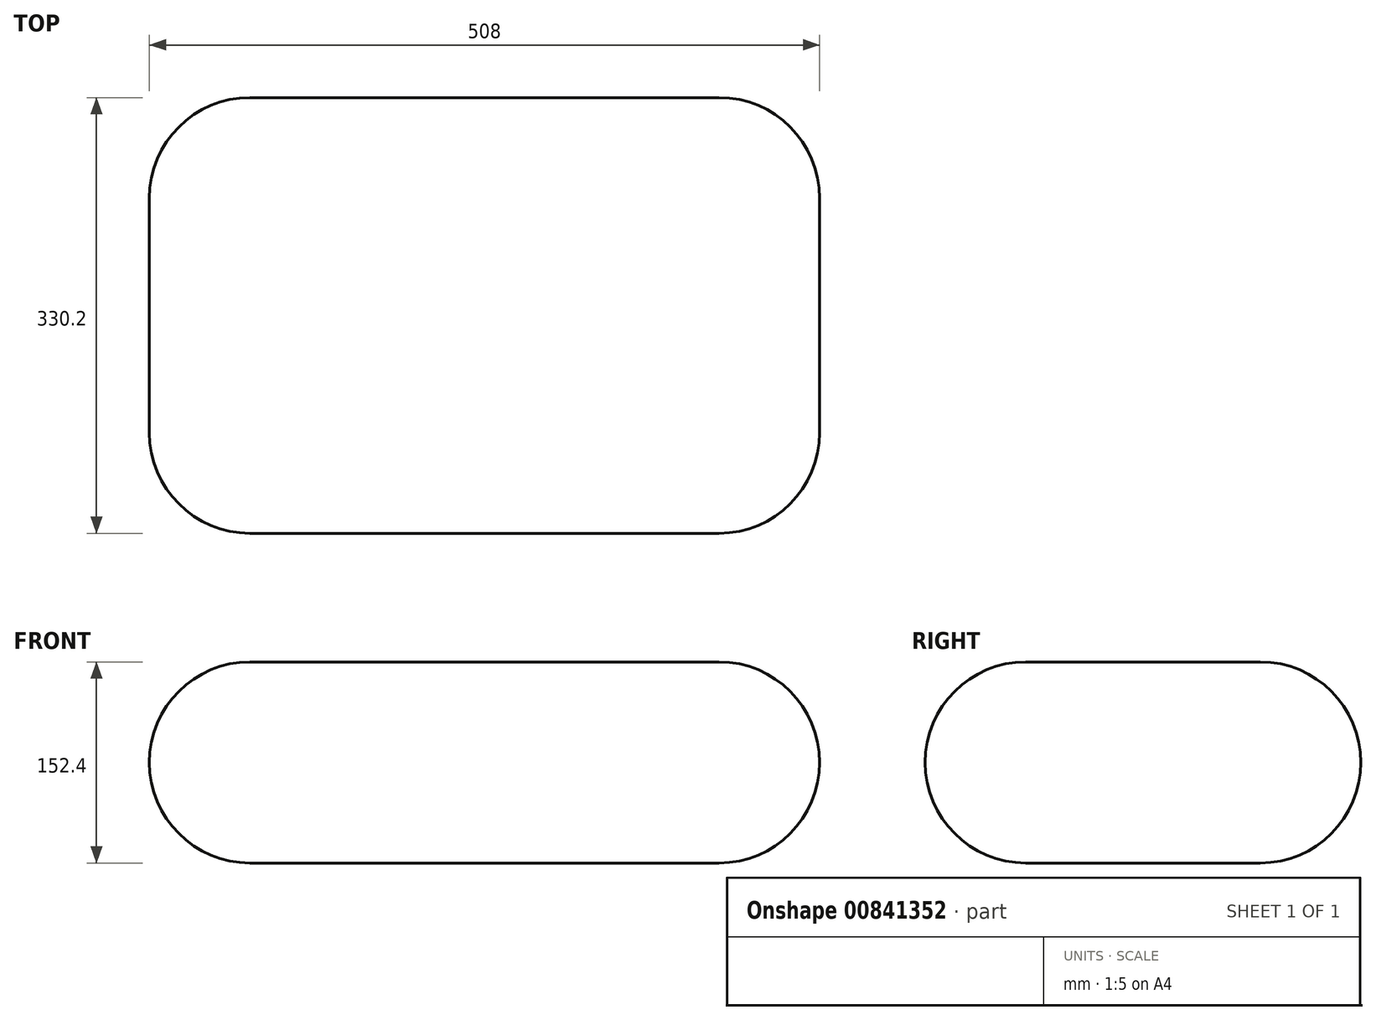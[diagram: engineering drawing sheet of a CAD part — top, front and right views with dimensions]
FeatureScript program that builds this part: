
annotation { "Feature Type Name" : "Feature", "Feature Type Description" : "" }
export const myFeature = defineFeature(function(context is Context, id is Id, definition is map)
    precondition{}
    {
        {
            var Q0;
            Q0=qCreatedBy(makeId("Top.planeOp"),FACE);
            var sketch = newSketch(context, id + "F0", { "sketchPlane" : qUnion([Q0])});
            skLineSegment(sketch, "E0.bottom", {"start": v(254, 165.1) * mm, "end": v(-254, 165.1) * mm});
            skLineSegment(sketch, "E0.top", {"start": v(254, -165.1) * mm, "end": v(-254, -165.1) * mm});
            skLineSegment(sketch, "E0.left", {"start": v(254, 165.1) * mm, "end": v(254, -165.1) * mm});
            skLineSegment(sketch, "E0.right", {"start": v(-254, 165.1) * mm, "end": v(-254, -165.1) * mm});
            skPoint(sketch, "E0.middle", {"position": v(0, 0) * mm});
            skSolve(sketch);
        }
        {
            var Q0;
            Q0 = qSketchRegion(id + "F0", true);
            extrude(context, id + "F1", {"entities" : qUnion([Q0]), "depth" : 152.4 * mm, "offsetDistance" : 25.4 * mm});
        }
        {
            var Q0;
            Q0=makeQuery(id+"F1.opExtrude","CAP_FACE",FACE,{"disambiguationData":[OSD([sQuery(id+"F0.wireOp",EDGE,"E0.bottom"),sQuery(id+"F0.wireOp",EDGE,"E0.top"),sQuery(id+"F0.wireOp",EDGE,"E0.left"),sQuery(id+"F0.wireOp",EDGE,"E0.right")])],"isStart":false});
            var Q1;
            Q1=makeQuery(id+"F1.opExtrude","SWEPT_FACE",FACE,{"disambiguationData":[OSD([sQuery(id+"F0.wireOp",EDGE,"E0.top")])]});
            var Q2;
            Q2=makeQuery(id+"F1.opExtrude","SWEPT_FACE",FACE,{"disambiguationData":[OSD([sQuery(id+"F0.wireOp",EDGE,"E0.left")])]});
            var Q3;
            Q3=makeQuery(id+"F1.opExtrude","SWEPT_FACE",FACE,{"disambiguationData":[OSD([sQuery(id+"F0.wireOp",EDGE,"E0.bottom")])]});
            var Q4;
            Q4=makeQuery(id+"F1.opExtrude","CAP_FACE",FACE,{"disambiguationData":[OSD([sQuery(id+"F0.wireOp",EDGE,"E0.bottom"),sQuery(id+"F0.wireOp",EDGE,"E0.top"),sQuery(id+"F0.wireOp",EDGE,"E0.left"),sQuery(id+"F0.wireOp",EDGE,"E0.right")])],"isStart":true});
            fillet(context, id + "F2", {"entities" : qUnion([Q0, Q1, Q2, Q3, Q4]), "radius" : 76.2 * mm, "tangentPropagation" : true, "allowEdgeOverflow" : false});
        }
    });
